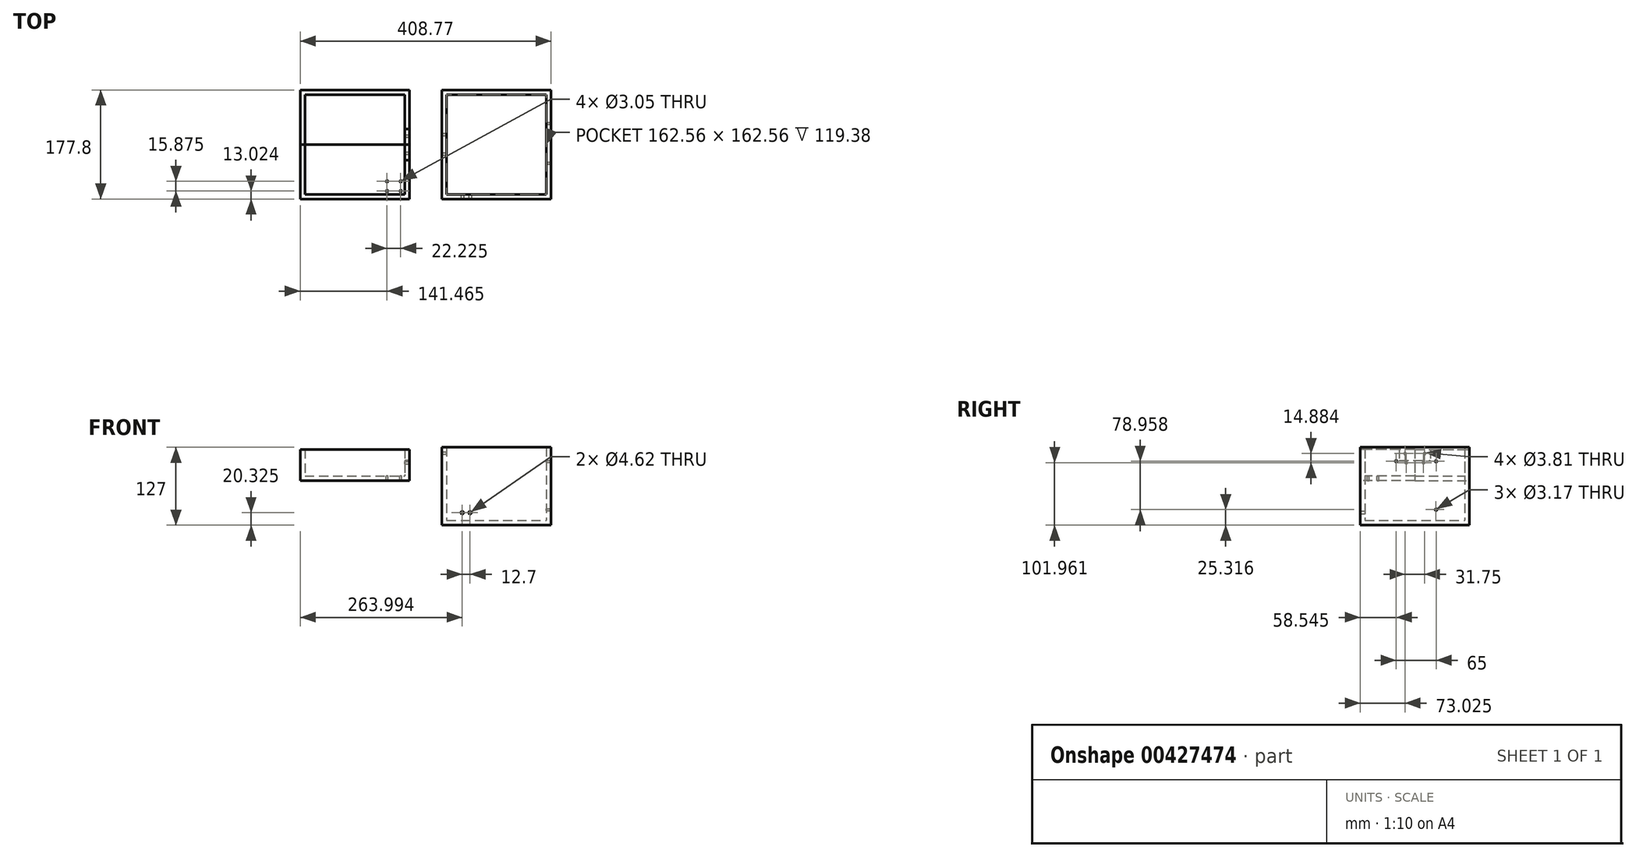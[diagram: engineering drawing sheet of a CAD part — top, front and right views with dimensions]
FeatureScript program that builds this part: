
annotation { "Feature Type Name" : "Feature", "Feature Type Description" : "" }
export const myFeature = defineFeature(function(context is Context, id is Id, definition is map)
    precondition{}
    {
        {
            var Q0;
            Q0=qCreatedBy(makeId("Front.planeOp"),FACE);
            var sketch = newSketch(context, id + "F0", { "sketchPlane" : qUnion([Q0])});
            skLineSegment(sketch, "E0.bottom", {"start": v(-88.64, 45.96) * mm, "end": v(89.16, 45.96) * mm});
            skLineSegment(sketch, "E0.top", {"start": v(-88.64, -81.04) * mm, "end": v(89.16, -81.04) * mm});
            skLineSegment(sketch, "E0.left", {"start": v(-88.64, 45.96) * mm, "end": v(-88.64, -81.04) * mm});
            skLineSegment(sketch, "E0.right", {"start": v(89.16, 45.96) * mm, "end": v(89.16, -81.04) * mm});
            skLineSegment(sketch, "E1", {"start": v(-81.02, 45.96) * mm, "end": v(-81.02, -73.42) * mm});
            skLineSegment(sketch, "E2", {"start": v(81.54, 45.96) * mm, "end": v(81.54, -73.42) * mm});
            skLineSegment(sketch, "E3", {"start": v(-81.02, -73.42) * mm, "end": v(81.54, -73.42) * mm});
            skPoint(sketch, "E4.orphan", {"position": v(89.16, -73.42) * mm});
            skSolve(sketch);
        }
        {
            var Q0;
            {var subQ0=sQuery(id+"F0.wireOp",EDGE,"E1");Q0=makeQuery(id+"F0.imprint","IMPRINT",FACE,{"disambiguationData":[TD([[makeQuery(id+"F0.imprint","IMPRINT",EDGE,{"derivedFrom":subQ0}),1.0]])]});}
            extrude(context, id + "F1", {"entities" : qUnion([Q0]), "depth" : 7.62 * mm});
        }
        {
            var Q0;
            Q0=makeQuery(id+"F0.imprint","IMPRINT",FACE,{"disambiguationData":[TD([[makeQuery(id+"F0.imprint","IMPRINT",EDGE,{"derivedFrom":sQuery(id+"F0.wireOp",EDGE,"E0.top")}),1.0]])]});
            extrude(context, id + "F2", {"entities" : qUnion([Q0]), "operationType" : NewBodyOperationType.ADD, "depth" : 88.9 * mm});
        }
        {
            var Q0;
            Q0=makeQuery(id+"F1.opExtrude","SWEPT_BODY",BODY,{"disambiguationData":[OSD([sQuery(id+"F0.wireOp",EDGE,"E0.bottom"),sQuery(id+"F0.wireOp",EDGE,"E1"),sQuery(id+"F0.wireOp",EDGE,"E2"),sQuery(id+"F0.wireOp",EDGE,"E3")])]});
            var Q1;
            Q1=makeQuery(id+"F2.opExtrude","CAP_FACE",FACE,{"disambiguationData":[OSD([sQuery(id+"F0.wireOp",EDGE,"E0.bottom"),sQuery(id+"F0.wireOp",EDGE,"E0.top"),sQuery(id+"F0.wireOp",EDGE,"E0.left"),sQuery(id+"F0.wireOp",EDGE,"E0.right"),sQuery(id+"F0.wireOp",EDGE,"E1"),sQuery(id+"F0.wireOp",EDGE,"E2"),sQuery(id+"F0.wireOp",EDGE,"E3")])],"isStart":false});
            mirror(context, id + "F3", {"operationType" : NewBodyOperationType.ADD, "entities" : qUnion([Q0]), "mirrorPlane" : qUnion([Q1])});
        }
        {
            var Q0;
            Q0=qCreatedBy(makeId("Front.planeOp"),FACE);
            var sketch = newSketch(context, id + "F4", { "sketchPlane" : qUnion([Q0])});
            skLineSegment(sketch, "E5.bottom", {"start": v(-319.61, 42.51) * mm, "end": v(-141.81, 42.51) * mm});
            skLineSegment(sketch, "E5.top", {"start": v(-319.61, -8.29) * mm, "end": v(-141.81, -8.29) * mm});
            skLineSegment(sketch, "E5.left", {"start": v(-319.61, 42.51) * mm, "end": v(-319.61, -8.29) * mm});
            skLineSegment(sketch, "E5.right", {"start": v(-141.81, 42.51) * mm, "end": v(-141.81, -8.29) * mm});
            skLineSegment(sketch, "E6", {"start": v(-312, 42.51) * mm, "end": v(-312, -0.67) * mm});
            skLineSegment(sketch, "E7", {"start": v(-312, -0.67) * mm, "end": v(-149.43, -0.67) * mm});
            skLineSegment(sketch, "E8", {"start": v(-149.43, 42.51) * mm, "end": v(-149.43, -0.67) * mm});
            skSolve(sketch);
        }
        {
            var Q0;
            {var subQ0=sQuery(id+"F4.wireOp",EDGE,"E6");Q0=makeQuery(id+"F4.imprint","IMPRINT",FACE,{"disambiguationData":[TD([[makeQuery(id+"F4.imprint","IMPRINT",EDGE,{"derivedFrom":subQ0}),1.0]])]});}
            extrude(context, id + "F5", {"entities" : qUnion([Q0]), "depth" : 7.62 * mm});
        }
        {
            var Q0;
            Q0=makeQuery(id+"F4.imprint","IMPRINT",FACE,{"disambiguationData":[TD([[makeQuery(id+"F4.imprint","IMPRINT",EDGE,{"derivedFrom":sQuery(id+"F4.wireOp",EDGE,"E5.top")}),1.0]])]});
            extrude(context, id + "F6", {"entities" : qUnion([Q0]), "operationType" : NewBodyOperationType.ADD, "depth" : 88.9 * mm});
        }
        {
            var Q0;
            Q0=makeQuery(id+"F5.opExtrude","SWEPT_BODY",BODY,{"disambiguationData":[OSD([sQuery(id+"F4.wireOp",EDGE,"E5.bottom"),sQuery(id+"F4.wireOp",EDGE,"E6"),sQuery(id+"F4.wireOp",EDGE,"E7"),sQuery(id+"F4.wireOp",EDGE,"E8")])]});
            var Q1;
            Q1=makeQuery(id+"F6.opExtrude","CAP_FACE",FACE,{"disambiguationData":[OSD([sQuery(id+"F4.wireOp",EDGE,"E5.bottom"),sQuery(id+"F4.wireOp",EDGE,"E5.top"),sQuery(id+"F4.wireOp",EDGE,"E5.left"),sQuery(id+"F4.wireOp",EDGE,"E5.right"),sQuery(id+"F4.wireOp",EDGE,"E6"),sQuery(id+"F4.wireOp",EDGE,"E7"),sQuery(id+"F4.wireOp",EDGE,"E8")])],"isStart":false});
            mirror(context, id + "F7", {"operationType" : NewBodyOperationType.ADD, "entities" : qUnion([Q0]), "mirrorPlane" : qUnion([Q1])});
        }
        {
            var Q0;
            {var subQ0=sQuery(id+"F0.wireOp",EDGE,"E3");var subQ1=sQuery(id+"F0.wireOp",EDGE,"E2");var subQ2=sQuery(id+"F0.wireOp",EDGE,"E1");var subQ3=sQuery(id+"F0.wireOp",EDGE,"E0.bottom");Q0=makeQuery(id+"F3.opPattern","COPY",FACE,{"derivedFrom":makeQuery(id+"F2.boolean.opBoolean","MERGE",FACE,{"derivedFrom":[makeQuery(id+"F1.opExtrude","CAP_FACE",FACE,{"disambiguationData":[OSD([subQ3,subQ2,subQ1,subQ0])],"isStart":true}),makeQuery(id+"F2.opExtrude","CAP_FACE",FACE,{"disambiguationData":[OSD([subQ3,sQuery(id+"F0.wireOp",EDGE,"E0.top"),sQuery(id+"F0.wireOp",EDGE,"E0.left"),sQuery(id+"F0.wireOp",EDGE,"E0.right"),subQ2,subQ1,subQ0])],"isStart":true})]}),"instanceName":"1"});}
            var sketch = newSketch(context, id + "F8", { "sketchPlane" : qUnion([Q0])});
            skCircle(sketch, "E9", {"center": v(-55.62, -60.72) * mm, "radius": 2.31 * mm});
            skCircle(sketch, "E10", {"center": v(-42.92, -60.72) * mm, "radius": 2.31 * mm});
            skSolve(sketch);
        }
        {
            var Q0;
            Q0=makeQuery(id+"F8.imprint","IMPRINT",FACE,{"disambiguationData":[TD([[makeQuery(id+"F8.imprint","IMPRINT",EDGE,{"derivedFrom":sQuery(id+"F8.wireOp",EDGE,"E9")}),1.0]])]});
            var Q1;
            Q1=makeQuery(id+"F8.imprint","IMPRINT",FACE,{"disambiguationData":[TD([[makeQuery(id+"F8.imprint","IMPRINT",EDGE,{"derivedFrom":sQuery(id+"F8.wireOp",EDGE,"E10")}),1.0]])]});
            extrude(context, id + "F9", {"entities" : qUnion([Q0, Q1]), "operationType" : NewBodyOperationType.REMOVE, "oppositeDirection" : true, "depth" : 25.4 * mm});
        }
        {
            var Q0;
            {var subQ0=makeQuery(id+"F2.opExtrude","SWEPT_FACE",FACE,{"disambiguationData":[OSD([sQuery(id+"F0.wireOp",EDGE,"E0.left")])]});Q0=makeQuery(id+"F3.boolean.opBoolean","MERGE",FACE,{"derivedFrom":[subQ0,makeQuery(id+"F3.opPattern","COPY",FACE,{"derivedFrom":subQ0,"instanceName":"1"})]});}
            var sketch = newSketch(context, id + "F10", { "sketchPlane" : qUnion([Q0])});
            skCircle(sketch, "E11", {"center": v(73.03, 35.8) * mm, "radius": 1.9 * mm});
            skCircle(sketch, "E12", {"center": v(104.78, 35.8) * mm, "radius": 1.9 * mm});
            skSolve(sketch);
        }
        {
            var Q0;
            Q0=makeQuery(id+"F10.imprint","IMPRINT",FACE,{"disambiguationData":[TD([[makeQuery(id+"F10.imprint","IMPRINT",EDGE,{"derivedFrom":sQuery(id+"F10.wireOp",EDGE,"E11")}),1.0]])]});
            var Q1;
            Q1=makeQuery(id+"F10.imprint","IMPRINT",FACE,{"disambiguationData":[TD([[makeQuery(id+"F10.imprint","IMPRINT",EDGE,{"derivedFrom":sQuery(id+"F10.wireOp",EDGE,"E12")}),1.0]])]});
            extrude(context, id + "F11", {"entities" : qUnion([Q0, Q1]), "operationType" : NewBodyOperationType.REMOVE, "oppositeDirection" : true, "depth" : 25.4 * mm});
        }
        {
            var Q0;
            {var subQ0=makeQuery(id+"F6.opExtrude","SWEPT_FACE",FACE,{"disambiguationData":[OSD([sQuery(id+"F4.wireOp",EDGE,"E5.right")])]});Q0=makeQuery(id+"F7.boolean.opBoolean","MERGE",FACE,{"derivedFrom":[subQ0,makeQuery(id+"F7.opPattern","COPY",FACE,{"derivedFrom":subQ0,"instanceName":"1"})]});}
            var sketch = newSketch(context, id + "F12", { "sketchPlane" : qUnion([Q0])});
            skLineSegment(sketch, "E13.bottom", {"start": v(-114.3, 42.51) * mm, "end": v(-63.5, 42.51) * mm});
            skLineSegment(sketch, "E13.top", {"start": v(-114.3, 24.73) * mm, "end": v(-63.5, 24.73) * mm});
            skLineSegment(sketch, "E13.left", {"start": v(-114.3, 42.51) * mm, "end": v(-114.3, 24.73) * mm});
            skLineSegment(sketch, "E13.right", {"start": v(-63.5, 42.51) * mm, "end": v(-63.5, 24.73) * mm});
            skLineSegment(sketch, "E14", {"start": v(-177.8, 42.51) * mm, "end": v(-114.3, 42.51) * mm});
            skLineSegment(sketch, "E15", {"start": v(-63.5, 42.51) * mm, "end": v(0, 42.51) * mm});
            skCircle(sketch, "E16", {"center": v(-102.69, 20.92) * mm, "radius": 1.9 * mm});
            skCircle(sketch, "E17", {"center": v(-74.86, 20.92) * mm, "radius": 1.9 * mm});
            skSolve(sketch);
        }
        {
            var Q0;
            Q0=makeQuery(id+"F12.imprint","IMPRINT",FACE,{"disambiguationData":[TD([[makeQuery(id+"F12.imprint","IMPRINT",EDGE,{"derivedFrom":sQuery(id+"F12.wireOp",EDGE,"E13.bottom")}),-1.0]])]});
            extrude(context, id + "F13", {"entities" : qUnion([Q0]), "operationType" : NewBodyOperationType.REMOVE, "oppositeDirection" : true, "depth" : 25.4 * mm});
        }
        {
            var Q0;
            Q0=makeQuery(id+"F12.imprint","IMPRINT",FACE,{"disambiguationData":[TD([[makeQuery(id+"F12.imprint","IMPRINT",EDGE,{"derivedFrom":sQuery(id+"F12.wireOp",EDGE,"E16")}),1.0]])]});
            var Q1;
            Q1=makeQuery(id+"F12.imprint","IMPRINT",FACE,{"disambiguationData":[TD([[makeQuery(id+"F12.imprint","IMPRINT",EDGE,{"derivedFrom":sQuery(id+"F12.wireOp",EDGE,"E17")}),1.0]])]});
            extrude(context, id + "F14", {"entities" : qUnion([Q0, Q1]), "operationType" : NewBodyOperationType.REMOVE, "oppositeDirection" : true, "depth" : 25.4 * mm});
        }
        {
            var Q0;
            {var subQ0=makeQuery(id+"F2.opExtrude","SWEPT_FACE",FACE,{"disambiguationData":[OSD([sQuery(id+"F0.wireOp",EDGE,"E0.right")])]});Q0=makeQuery(id+"F3.boolean.opBoolean","MERGE",FACE,{"derivedFrom":[subQ0,makeQuery(id+"F3.opPattern","COPY",FACE,{"derivedFrom":subQ0,"instanceName":"1"})]});}
            var sketch = newSketch(context, id + "F15", { "sketchPlane" : qUnion([Q0])});
            skLineSegment(sketch, "E18.bottom", {"start": v(-131.3, -61.81) * mm, "end": v(-131.3, 28.44) * mm});
            skLineSegment(sketch, "E18.top", {"start": v(-46.5, -61.81) * mm, "end": v(-46.5, 28.44) * mm});
            skLineSegment(sketch, "E18.left", {"start": v(-131.3, -61.81) * mm, "end": v(-46.5, -61.81) * mm});
            skLineSegment(sketch, "E18.right", {"start": v(-131.3, 28.44) * mm, "end": v(-46.5, 28.44) * mm});
            skPoint(sketch, "E19", {"position": v(-131.3, -16.69) * mm});
            skCircle(sketch, "E20", {"center": v(-119.25, 23.23) * mm, "radius": 1.59 * mm});
            skCircle(sketch, "E21", {"center": v(-54.25, 23.23) * mm, "radius": 1.59 * mm});
            skPoint(sketch, "E22", {"position": v(-88.9, 28.44) * mm});
            skCircle(sketch, "E23", {"center": v(-54.39, -55.72) * mm, "radius": 1.59 * mm});
            skPoint(sketch, "E24", {"position": v(-88.9, 45.96) * mm});
            skSolve(sketch);
        }
        {
            var Q0;
            Q0=makeQuery(id+"F15.imprint","IMPRINT",FACE,{"disambiguationData":[TD([[makeQuery(id+"F15.imprint","IMPRINT",EDGE,{"derivedFrom":sQuery(id+"F15.wireOp",EDGE,"E20")}),1.0]])]});
            var Q1;
            Q1=makeQuery(id+"F15.imprint","IMPRINT",FACE,{"disambiguationData":[TD([[makeQuery(id+"F15.imprint","IMPRINT",EDGE,{"derivedFrom":sQuery(id+"F15.wireOp",EDGE,"E21")}),1.0]])]});
            var Q2;
            Q2=makeQuery(id+"F15.imprint","IMPRINT",FACE,{"disambiguationData":[TD([[makeQuery(id+"F15.imprint","IMPRINT",EDGE,{"derivedFrom":sQuery(id+"F15.wireOp",EDGE,"E23")}),1.0]])]});
            extrude(context, id + "F16", {"entities" : qUnion([Q0, Q1, Q2]), "operationType" : NewBodyOperationType.REMOVE, "oppositeDirection" : true, "depth" : 25.4 * mm});
        }
        {
            var Q0;
            {var subQ0=makeQuery(id+"F6.opExtrude","SWEPT_FACE",FACE,{"disambiguationData":[OSD([sQuery(id+"F4.wireOp",EDGE,"E7")])]});Q0=makeQuery(id+"F7.boolean.opBoolean","MERGE",FACE,{"derivedFrom":[subQ0,makeQuery(id+"F7.opPattern","COPY",FACE,{"derivedFrom":subQ0,"instanceName":"1"})]});}
            var sketch = newSketch(context, id + "F17", { "sketchPlane" : qUnion([Q0])});
            skCircle(sketch, "E25", {"center": v(-155.92, -164.78) * mm, "radius": 1.52 * mm});
            skCircle(sketch, "E26", {"center": v(-178.15, -164.78) * mm, "radius": 1.52 * mm});
            skCircle(sketch, "E27", {"center": v(-155.92, -148.9) * mm, "radius": 1.52 * mm});
            skCircle(sketch, "E28", {"center": v(-178.15, -148.9) * mm, "radius": 1.52 * mm});
            skSolve(sketch);
        }
        {
            var Q0;
            Q0=makeQuery(id+"F17.imprint","IMPRINT",FACE,{"disambiguationData":[TD([[makeQuery(id+"F17.imprint","IMPRINT",EDGE,{"derivedFrom":sQuery(id+"F17.wireOp",EDGE,"E28")}),1.0]])]});
            var Q1;
            Q1=makeQuery(id+"F17.imprint","IMPRINT",FACE,{"disambiguationData":[TD([[makeQuery(id+"F17.imprint","IMPRINT",EDGE,{"derivedFrom":sQuery(id+"F17.wireOp",EDGE,"E27")}),1.0]])]});
            var Q2;
            Q2=makeQuery(id+"F17.imprint","IMPRINT",FACE,{"disambiguationData":[TD([[makeQuery(id+"F17.imprint","IMPRINT",EDGE,{"derivedFrom":sQuery(id+"F17.wireOp",EDGE,"E26")}),1.0]])]});
            var Q3;
            Q3=makeQuery(id+"F17.imprint","IMPRINT",FACE,{"disambiguationData":[TD([[makeQuery(id+"F17.imprint","IMPRINT",EDGE,{"derivedFrom":sQuery(id+"F17.wireOp",EDGE,"E25")}),1.0]])]});
            extrude(context, id + "F18", {"entities" : qUnion([Q0, Q1, Q2, Q3]), "operationType" : NewBodyOperationType.REMOVE, "oppositeDirection" : true, "depth" : 25.4 * mm});
        }
    });
